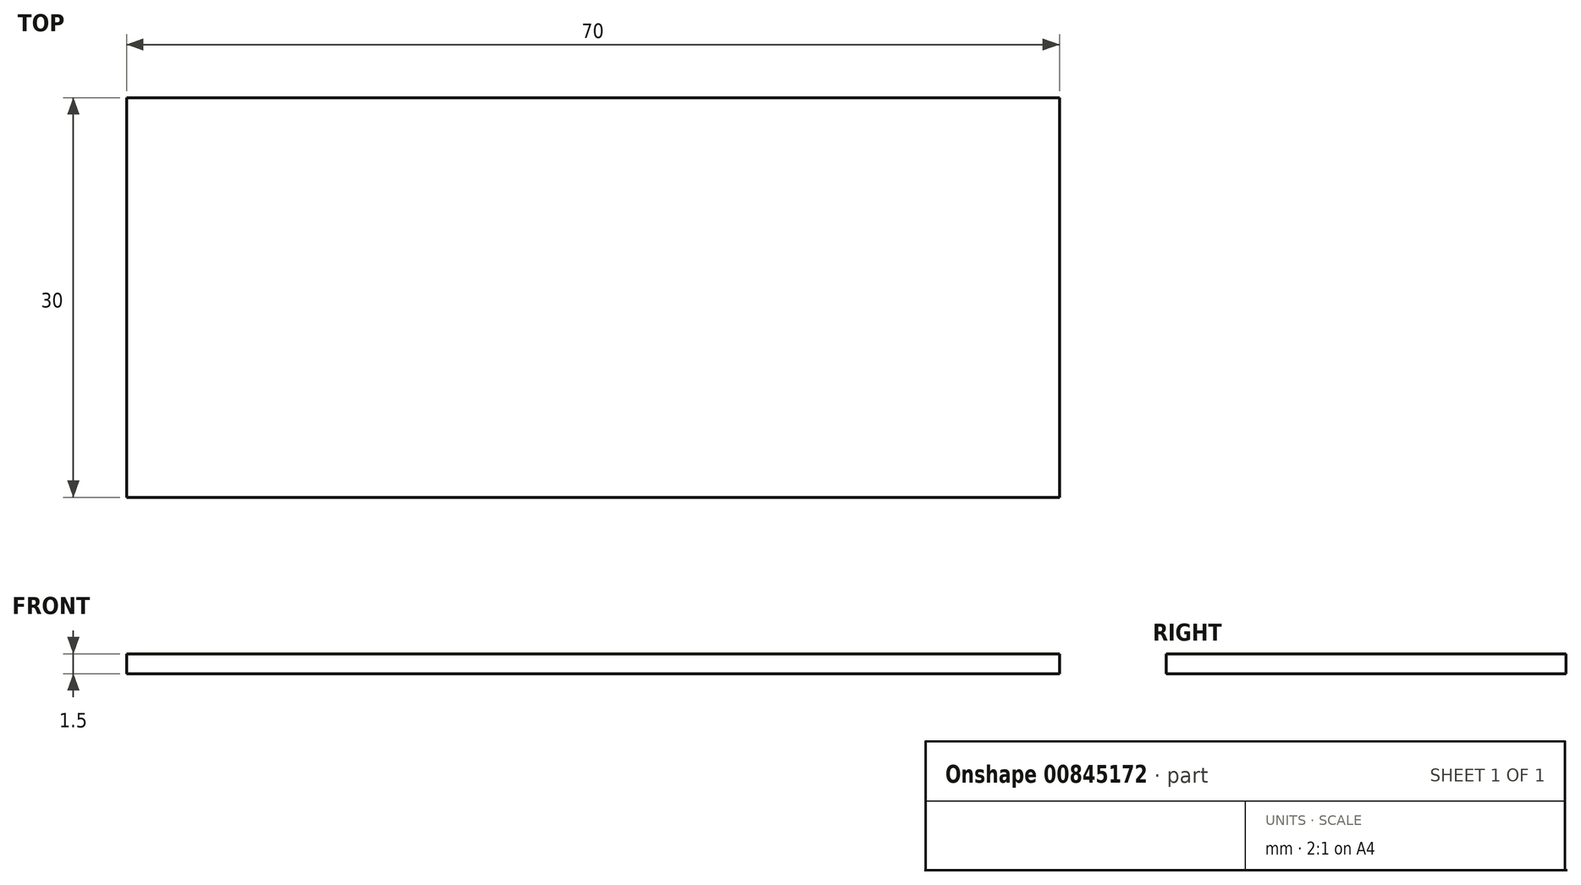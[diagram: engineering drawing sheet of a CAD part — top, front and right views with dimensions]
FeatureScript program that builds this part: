
annotation { "Feature Type Name" : "Feature", "Feature Type Description" : "" }
export const myFeature = defineFeature(function(context is Context, id is Id, definition is map)
    precondition{}
    {
        {
            var Q0;
            Q0=qCreatedBy(makeId("Top.planeOp"),FACE);
            var sketch = newSketch(context, id + "F0", { "sketchPlane" : qUnion([Q0])});
            skLineSegment(sketch, "E0.bottom", {"start": v(35, 15) * mm, "end": v(-35, 15) * mm});
            skLineSegment(sketch, "E0.top", {"start": v(35, -15) * mm, "end": v(-35, -15) * mm});
            skLineSegment(sketch, "E0.left", {"start": v(35, 15) * mm, "end": v(35, -15) * mm});
            skLineSegment(sketch, "E0.right", {"start": v(-35, 15) * mm, "end": v(-35, -15) * mm});
            skPoint(sketch, "E0.middle", {"position": v(0, 0) * mm});
            skSolve(sketch);
        }
        {
            var Q0;
            Q0=makeQuery(id+"F0.imprint","IMPRINT",FACE,{"disambiguationData":[TD([[makeQuery(id+"F0.imprint","IMPRINT",EDGE,{"derivedFrom":sQuery(id+"F0.wireOp",EDGE,"E0.bottom")}),1.0]])]});
            extrude(context, id + "F1", {"entities" : qUnion([Q0]), "depth" : 1.5 * mm, "offsetDistance" : 25 * mm});
        }
    });
